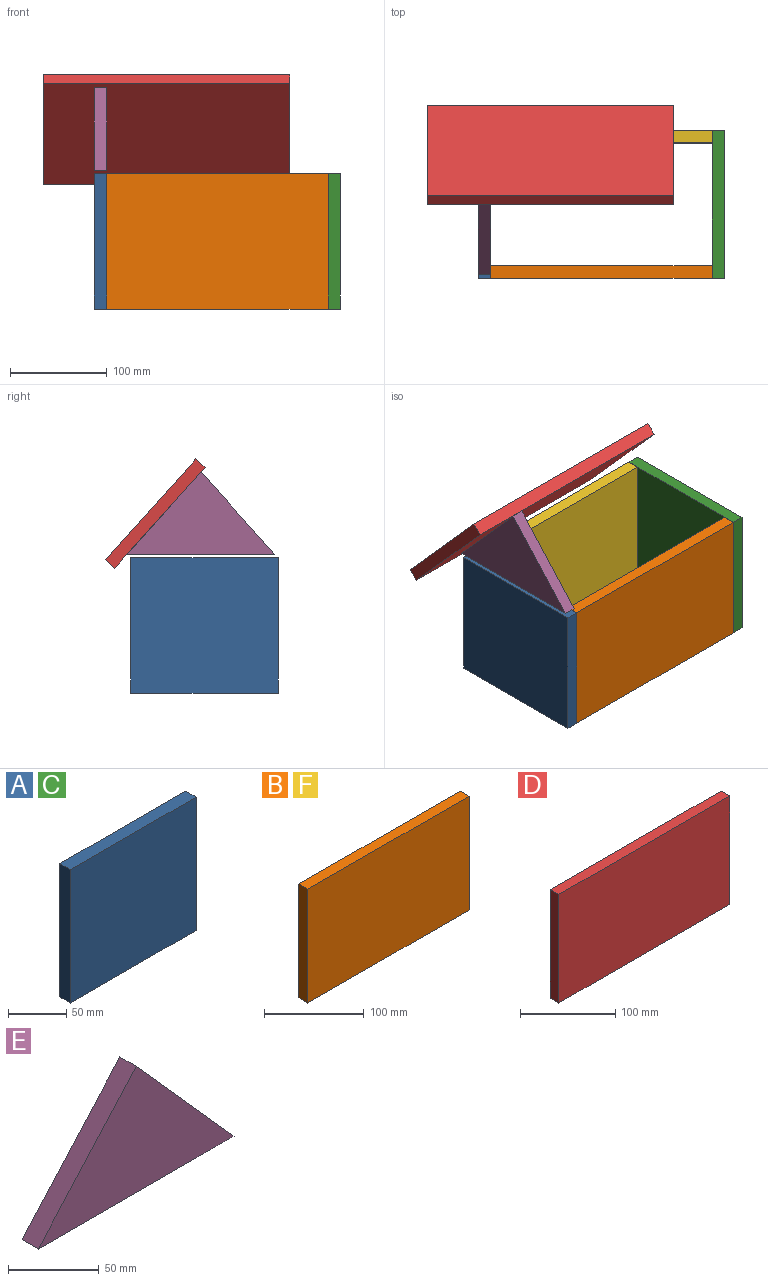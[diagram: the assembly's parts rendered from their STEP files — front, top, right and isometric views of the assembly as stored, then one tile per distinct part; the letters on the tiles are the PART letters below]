
ASSEMBLY  parts=6 mates=10
PART A: 6 faces, bbox 152.4x12.7x139.7 mm
  f0: plane 152.4x12.7mm, normal (0,0,1), area 1935.5mm2, adj f1,f3,f4,f5
  f1: plane 139.7x12.7mm, normal (-1,0,0), area 1774.2mm2, adj f0,f2,f4,f5
  f2: plane 152.4x12.7mm, normal (0,0,-1), area 1935.5mm2, adj f1,f3,f4,f5
  f3: plane 139.7x12.7mm, normal (1,0,0), area 1774.2mm2, adj f0,f2,f4,f5
  f4: plane 152.4x139.7mm, normal (0,-1,0), area 21290.3mm2, adj f0,f1,f2,f3
  f5: plane 152.4x139.7mm, normal (0,1,0), area 21290.3mm2, adj f0,f1,f2,f3
PART B: 6 faces, bbox 228.6x12.7x139.7 mm
  f0: plane 228.6x12.7mm, normal (0,0,1), area 2903.2mm2, adj f1,f3,f4,f5
  f1: plane 139.7x12.7mm, normal (-1,0,0), area 1774.2mm2, adj f0,f2,f4,f5
  f2: plane 228.6x12.7mm, normal (0,0,-1), area 2903.2mm2, adj f1,f3,f4,f5
  f3: plane 139.7x12.7mm, normal (1,0,0), area 1774.2mm2, adj f0,f2,f4,f5
  f4: plane 228.6x139.7mm, normal (0,-1,0), area 31935.4mm2, adj f0,f1,f2,f3
  f5: plane 228.6x139.7mm, normal (0,1,0), area 31935.4mm2, adj f0,f1,f2,f3
PART C: same geometry as A
PART D: 6 faces, bbox 254x12.7x139.7 mm
  f0: plane 254x12.7mm, normal (0,0,1), area 3225.8mm2, adj f1,f3,f4,f5
  f1: plane 139.7x12.7mm, normal (-1,0,0), area 1774.2mm2, adj f0,f2,f4,f5
  f2: plane 254x12.7mm, normal (0,0,-1), area 3225.8mm2, adj f1,f3,f4,f5
  f3: plane 139.7x12.7mm, normal (1,0,0), area 1774.2mm2, adj f0,f2,f4,f5
  f4: plane 254x139.7mm, normal (0,-1,0), area 35483.8mm2, adj f0,f1,f2,f3
  f5: plane 254x139.7mm, normal (0,1,0), area 35483.8mm2, adj f0,f1,f2,f3
PART E: 5 faces, bbox 152.4x12.7x85.2 mm
  f0: plane 85.19x76.2mm, normal (-0.75,0,0.67), area 1451.6mm2, adj f1,f2,f3,f4
  f1: plane 152.4x12.7mm, normal (0,0,-1), area 1935.5mm2, adj f0,f2,f3,f4
  f2: plane 85.19x76.2mm, normal (0.75,0,0.67), area 1451.6mm2, adj f0,f1,f3,f4
  f3: plane 152.4x85.19mm, normal (0,-1,0), area 6491.8mm2, adj f0,f1,f2
  f4: plane 152.4x85.19mm, normal (0,1,0), area 6491.8mm2, adj f0,f1,f2
PART F: same geometry as B
PLACE A rot(axis=(-0.71,-0.71,0),180deg) t=(-167.32,-63.5,-59.39)mm
PLACE B t=(-53.02,-127,-59.39)mm
PLACE C rot(axis=(0,0,1),90deg) t=(61.28,-63.5,-59.39)mm
PLACE D rot(axis=(1,0,0),41.8deg) t=(-105.35,-7.95,60.3)mm
PLACE E rot(axis=(0,0,-1),90deg) t=(-167.32,-59.73,66.42)mm
PLACE F t=(-53.02,12.7,-59.39)mm fixed
MATE planar A.f3 <-> F.f5  axis (0,1,0) through (-173.67,12.7,-59.39)mm
MATE planar C.f2 <-> B.f2  axis (0,0,-1) through (67.63,-63.5,-129.24)mm
MATE planar D.f4 <-> E.f0  axis (0,-0.75,-0.67) through (-105.35,-17.42,51.84)mm
MATE planar F.f2 <-> B.f2  axis (0,0,-1) through (-53.02,6.35,-129.24)mm
MATE planar A.f5 <-> B.f1  axis (1,0,0) through (-167.32,-63.5,-59.39)mm
MATE planar E.f3 <-> A.f4  axis (-1,0,0) through (-180.02,-59.73,42.34)mm
MATE planar F.f1 <-> A.f5  axis (-1,0,0) through (-167.32,6.35,-59.39)mm
MATE planar B.f3 <-> C.f5  axis (1,0,0) through (61.28,-133.35,-59.39)mm
MATE planar B.f4 <-> A.f1  axis (0,-1,0) through (-53.02,-139.7,-59.39)mm
MATE planar B.f4 <-> C.f1  axis (0,-1,0) through (-53.02,-139.7,-59.39)mm
